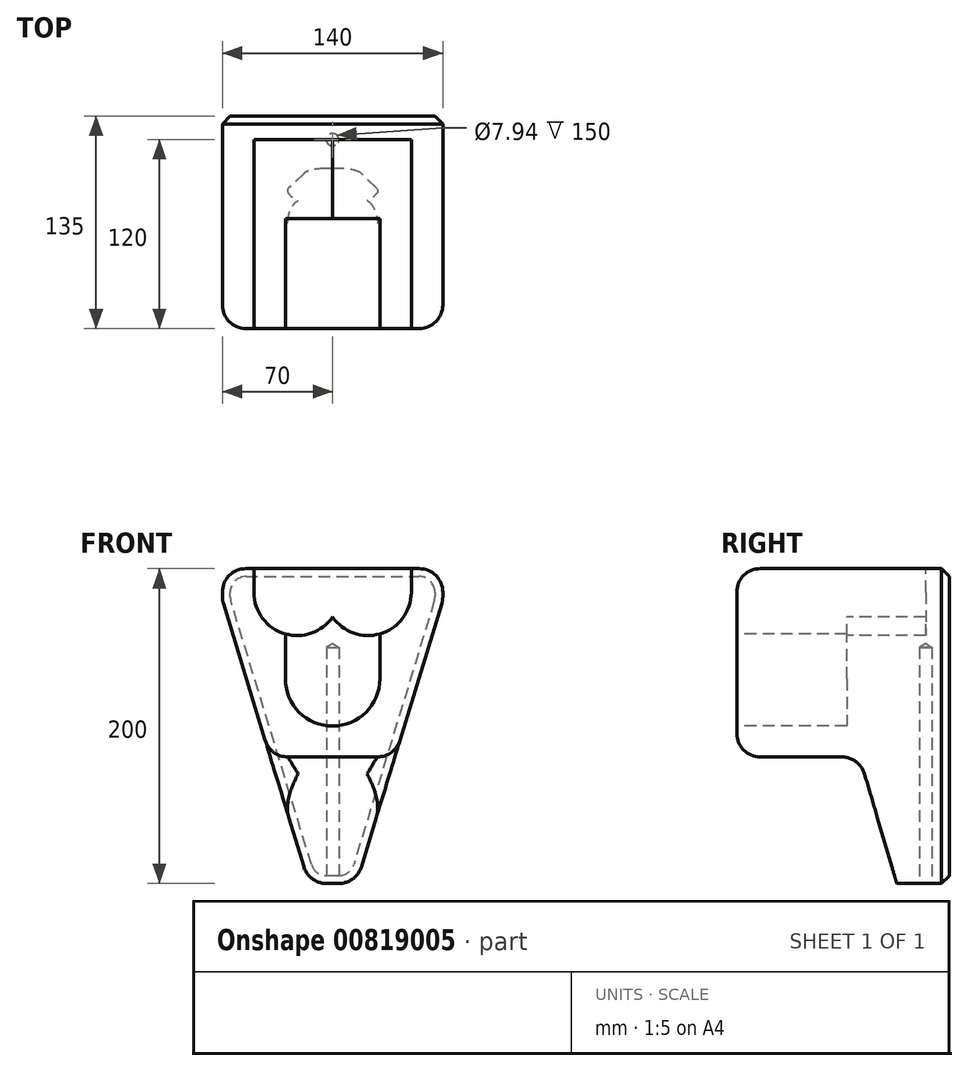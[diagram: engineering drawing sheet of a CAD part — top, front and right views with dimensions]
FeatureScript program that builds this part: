
annotation { "Feature Type Name" : "Feature", "Feature Type Description" : "" }
export const myFeature = defineFeature(function(context is Context, id is Id, definition is map)
    precondition{}
    {
        {
            var Q0;
            Q0=qCreatedBy(makeId("Front.planeOp"),FACE);
            var sketch = newSketch(context, id + "F0", { "sketchPlane" : qUnion([Q0])});
            skLineSegment(sketch, "E0.bottom", {"start": v(70, 70) * mm, "end": v(-70, 70) * mm});
            skLineSegment(sketch, "E0.left", {"start": v(70, 70) * mm, "end": v(70, 50) * mm});
            skLineSegment(sketch, "E0.right", {"start": v(-70, 70) * mm, "end": v(-70, 50) * mm});
            skPoint(sketch, "E0.middle", {"position": v(0, 60) * mm});
            skLineSegment(sketch, "E1", {"start": v(-70, 50) * mm, "end": v(-15, -130) * mm});
            skLineSegment(sketch, "E2", {"start": v(-15, -130) * mm, "end": v(15, -130) * mm});
            skLineSegment(sketch, "E3", {"start": v(15, -130) * mm, "end": v(70, 50) * mm});
            skSolve(sketch);
        }
        {
            var Q0;
            Q0=makeQuery(id+"F0.imprint","IMPRINT",FACE,{"disambiguationData":[TD([[makeQuery(id+"F0.imprint","IMPRINT",EDGE,{"derivedFrom":sQuery(id+"F0.wireOp",EDGE,"E0.bottom")}),1.0]])]});
            extrude(context, id + "F1", {"entities" : qUnion([Q0]), "depth" : 135 * mm, "offsetDistance" : 25 * mm});
        }
        {
            var Q0;
            Q0=makeQuery(id+"F1.opExtrude","CAP_FACE",FACE,{"disambiguationData":[OSD([sQuery(id+"F0.wireOp",EDGE,"E0.bottom"),sQuery(id+"F0.wireOp",EDGE,"E0.left"),sQuery(id+"F0.wireOp",EDGE,"E0.right"),sQuery(id+"F0.wireOp",EDGE,"E1"),sQuery(id+"F0.wireOp",EDGE,"E2"),sQuery(id+"F0.wireOp",EDGE,"E3")])],"isStart":false});
            var sketch = newSketch(context, id + "F2", { "sketchPlane" : qUnion([Q0])});
            skCircle(sketch, "E4", {"center": v(-22.5, 55) * mm, "radius": 27.5 * mm, "construction": true});
            skCircle(sketch, "E5.MirrorC", {"center": v(22.5, 55) * mm, "radius": 27.5 * mm, "construction": true});
            skLineSegment(sketch, "E6", {"start": v(-50, 55) * mm, "end": v(-50, 110) * mm});
            skLineSegment(sketch, "E7", {"start": v(-50, 110) * mm, "end": v(50, 110) * mm});
            skLineSegment(sketch, "E8", {"start": v(50, 110) * mm, "end": v(50, 55) * mm});
            skArc(sketch, "E9", {"start": v(-50, 55) * mm, "mid": v(-30.8, 28.78) * mm, "end": v(0, 39.19) * mm});
            skArc(sketch, "E10", {"start": v(0, 39.19) * mm, "mid": v(30.8, 28.78) * mm, "end": v(50, 55) * mm});
            skSolve(sketch);
        }
        {
            var Q0;
            Q0 = qSketchRegion(id + "F2", true);
            extrude(context, id + "F3", {"entities" : qUnion([Q0]), "operationType" : NewBodyOperationType.REMOVE, "oppositeDirection" : true, "depth" : 120 * mm, "offsetDistance" : 25 * mm});
        }
        {
            var Q0;
            Q0=makeQuery(id+"F1.opExtrude","SWEPT_EDGE",EDGE,{"disambiguationData":[OSD([sQuery(id+"F0.wireOp",EDGE,"E0.bottom"),sQuery(id+"F0.wireOp",EDGE,"E0.right")])]});
            var Q1;
            Q1=makeQuery(id+"F1.opExtrude","SWEPT_EDGE",EDGE,{"disambiguationData":[OSD([sQuery(id+"F0.wireOp",EDGE,"E0.bottom"),sQuery(id+"F0.wireOp",EDGE,"E0.left")])]});
            var Q2;
            Q2=makeQuery(id+"F1.opExtrude","SWEPT_EDGE",EDGE,{"disambiguationData":[OSD([sQuery(id+"F0.wireOp",EDGE,"E0.right"),sQuery(id+"F0.wireOp",EDGE,"E1")])]});
            var Q3;
            Q3=makeQuery(id+"F1.opExtrude","SWEPT_EDGE",EDGE,{"disambiguationData":[OSD([sQuery(id+"F0.wireOp",EDGE,"E0.left"),sQuery(id+"F0.wireOp",EDGE,"E3")])]});
            var Q4;
            Q4=makeQuery(id+"F1.opExtrude","SWEPT_EDGE",EDGE,{"disambiguationData":[OSD([sQuery(id+"F0.wireOp",EDGE,"E1"),sQuery(id+"F0.wireOp",EDGE,"E2")])]});
            var Q5;
            Q5=makeQuery(id+"F1.opExtrude","SWEPT_EDGE",EDGE,{"disambiguationData":[OSD([sQuery(id+"F0.wireOp",EDGE,"E2"),sQuery(id+"F0.wireOp",EDGE,"E3")])]});
            fillet(context, id + "F4", {"entities" : qUnion([Q0, Q1, Q2, Q3, Q4, Q5]), "radius" : 15 * mm, "tangentPropagation" : true, "allowEdgeOverflow" : false});
        }
        {
            var Q0;
            Q0=makeQuery(id+"F1.opExtrude","SWEPT_FACE",FACE,{"disambiguationData":[OSD([sQuery(id+"F0.wireOp",EDGE,"E2")])]});
            var sketch = newSketch(context, id + "F5", { "sketchPlane" : qUnion([Q0])});
            skCircle(sketch, "E11", {"center": v(0, 15) * mm, "radius": 7.5 * mm, "construction": true});
            skSolve(sketch);
        }
        {
            var Q0;
            Q0=sQuery(id+"F5.wireOp",VERTEX,"E11.center");
            var Q1;
            Q1=makeQuery(id+"F1.opExtrude","SWEPT_BODY",BODY,{"disambiguationData":[OSD([sQuery(id+"F0.wireOp",EDGE,"E0.bottom"),sQuery(id+"F0.wireOp",EDGE,"E0.left"),sQuery(id+"F0.wireOp",EDGE,"E0.right"),sQuery(id+"F0.wireOp",EDGE,"E1"),sQuery(id+"F0.wireOp",EDGE,"E2"),sQuery(id+"F0.wireOp",EDGE,"E3")])]});
            hole(context, id + "F6", {"style" : HoleStyle.SIMPLE, "endStyle" : HoleEndStyle.BLIND, "standardTappedOrClearance" : lookupTablePath({ "standard" : "ANSI", "engagement" : "75%", "pitch" : "16 tpi", "size" : "3/8", "type" : "Tapped" }), "standardBlindInLast" : lookupTablePath({ "standard" : "ANSI", "engagement" : "75%", "pitch" : "16 tpi", "size" : "3/8", "type" : "Tapped" }), "holeDiameter" : 7.94 * mm, "majorDiameter" : 9.52 * mm, "showTappedDepth" : true, "holeDepth" : 150 * mm, "isTappedThrough" : true, "tappedDepth" : 145.24 * mm, "tapClearance" : 3, "locations" : qUnion([Q0]), "scope" : qUnion([Q1])});
        }
        {
            var Q0;
            Q0=makeQuery(id+"F1.opExtrude","CAP_FACE",FACE,{"disambiguationData":[OSD([sQuery(id+"F0.wireOp",EDGE,"E0.bottom"),sQuery(id+"F0.wireOp",EDGE,"E0.left"),sQuery(id+"F0.wireOp",EDGE,"E0.right"),sQuery(id+"F0.wireOp",EDGE,"E1"),sQuery(id+"F0.wireOp",EDGE,"E2"),sQuery(id+"F0.wireOp",EDGE,"E3")])],"isStart":false});
            var sketch = newSketch(context, id + "F7", { "sketchPlane" : qUnion([Q0])});
            skCircle(sketch, "E12", {"center": v(0, 0) * mm, "radius": 30 * mm, "construction": true});
            skLineSegment(sketch, "E13", {"start": v(-30, 0) * mm, "end": v(-30, 100) * mm});
            skLineSegment(sketch, "E14", {"start": v(-30, 100) * mm, "end": v(30, 100) * mm});
            skLineSegment(sketch, "E15", {"start": v(30, 100) * mm, "end": v(30, 0) * mm});
            skArc(sketch, "E16", {"start": v(-30, 0) * mm, "mid": v(0, -30) * mm, "end": v(30, 0) * mm});
            skSolve(sketch);
        }
        {
            var Q0;
            Q0 = qSketchRegion(id + "F7", true);
            extrude(context, id + "F8", {"entities" : qUnion([Q0]), "operationType" : NewBodyOperationType.REMOVE, "oppositeDirection" : true, "depth" : 70 * mm, "offsetDistance" : 25 * mm});
        }
        {
            var Q0;
            Q0=qCreatedBy(makeId("Right.planeOp"),FACE);
            var sketch = newSketch(context, id + "F9", { "sketchPlane" : qUnion([Q0])});
            skLineSegment(sketch, "E17.bottom", {"start": v(-30.5, -139.58) * mm, "end": v(-175.25, -139.58) * mm});
            skLineSegment(sketch, "E18.bottom", {"start": v(-158.13, -49.6) * mm, "end": v(-57, -49.6) * mm});
            skLineSegment(sketch, "E19", {"start": v(-30.5, -139.58) * mm, "end": v(-57, -49.6) * mm});
            skLineSegment(sketch, "E20", {"start": v(-158.13, -49.6) * mm, "end": v(-175.25, -139.58) * mm});
            skSolve(sketch);
        }
        {
            var Q0;
            Q0=makeQuery(id+"F9.imprint","IMPRINT",FACE,{"disambiguationData":[TD([[makeQuery(id+"F9.imprint","IMPRINT",EDGE,{"derivedFrom":sQuery(id+"F9.wireOp",EDGE,"E17.bottom")}),-1.0]])]});
            extrude(context, id + "F10", {"entities" : qUnion([Q0]), "operationType" : NewBodyOperationType.REMOVE, "endBound" : BoundingType.THROUGH_ALL, "oppositeDirection" : true, "depth" : 25 * mm, "offsetDistance" : 25 * mm, "hasSecondDirection" : true, "secondDirectionBound" : SecondDirectionBoundingType.THROUGH_ALL, "secondDirectionOppositeDirection" : false, "secondDirectionDepth" : 25 * mm});
        }
        {
            var Q0;
            Q0=makeQuery(id+"F10.boolean.opBoolean","COPY",FACE,{"derivedFrom":makeQuery(id+"F10.opExtrude","SWEPT_FACE",FACE,{"disambiguationData":[OSD([sQuery(id+"F9.wireOp",EDGE,"E18.bottom")])]})});
            fillet(context, id + "F11", {"entities" : qUnion([Q0]), "radius" : 15 * mm, "tangentPropagation" : true, "allowEdgeOverflow" : false});
        }
        {
            var Q0;
            Q0=makeQuery(id+"F1.opExtrude","CAP_FACE",FACE,{"disambiguationData":[OSD([sQuery(id+"F0.wireOp",EDGE,"E0.bottom"),sQuery(id+"F0.wireOp",EDGE,"E0.left"),sQuery(id+"F0.wireOp",EDGE,"E0.right"),sQuery(id+"F0.wireOp",EDGE,"E1"),sQuery(id+"F0.wireOp",EDGE,"E2"),sQuery(id+"F0.wireOp",EDGE,"E3")])],"isStart":true});
            chamfer(context, id + "F12", {"entities" : qUnion([Q0]), "width" : 5 * mm, "tangentPropagation" : true});
        }
        {
            var Q0;
            {var subQ0=sQuery(id+"F0.wireOp",EDGE,"E0.left");var subQ1=sQuery(id+"F0.wireOp",EDGE,"E0.bottom");Q0=makeQuery(id+"F4.opFillet","BLEND_EDGE",EDGE,{"blendedFrom":[makeQuery(id+"F1.opExtrude","SWEPT_EDGE",EDGE,{"disambiguationData":[OSD([subQ1,subQ0])]}),makeQuery(id+"F1.opExtrude","CAP_FACE",FACE,{"disambiguationData":[OSD([subQ1,subQ0,sQuery(id+"F0.wireOp",EDGE,"E0.right"),sQuery(id+"F0.wireOp",EDGE,"E1"),sQuery(id+"F0.wireOp",EDGE,"E2"),sQuery(id+"F0.wireOp",EDGE,"E3")])],"isStart":false})],"blendedInto":[makeQuery(id+"F1.opExtrude","CAP_FACE",FACE,{"disambiguationData":[OSD([subQ1,subQ0,sQuery(id+"F0.wireOp",EDGE,"E0.right"),sQuery(id+"F0.wireOp",EDGE,"E1"),sQuery(id+"F0.wireOp",EDGE,"E2"),sQuery(id+"F0.wireOp",EDGE,"E3")])],"isStart":false})]});}
            var Q1;
            {var subQ0=sQuery(id+"F0.wireOp",EDGE,"E0.right");var subQ1=sQuery(id+"F0.wireOp",EDGE,"E0.bottom");Q1=makeQuery(id+"F4.opFillet","BLEND_EDGE",EDGE,{"blendedFrom":[makeQuery(id+"F1.opExtrude","SWEPT_EDGE",EDGE,{"disambiguationData":[OSD([subQ1,subQ0])]}),makeQuery(id+"F1.opExtrude","CAP_FACE",FACE,{"disambiguationData":[OSD([subQ1,sQuery(id+"F0.wireOp",EDGE,"E0.left"),subQ0,sQuery(id+"F0.wireOp",EDGE,"E1"),sQuery(id+"F0.wireOp",EDGE,"E2"),sQuery(id+"F0.wireOp",EDGE,"E3")])],"isStart":false})],"blendedInto":[makeQuery(id+"F1.opExtrude","CAP_FACE",FACE,{"disambiguationData":[OSD([subQ1,sQuery(id+"F0.wireOp",EDGE,"E0.left"),subQ0,sQuery(id+"F0.wireOp",EDGE,"E1"),sQuery(id+"F0.wireOp",EDGE,"E2"),sQuery(id+"F0.wireOp",EDGE,"E3")])],"isStart":false})]});}
            fillet(context, id + "F13", {"entities" : qUnion([Q0, Q1]), "radius" : 15 * mm, "tangentPropagation" : true, "allowEdgeOverflow" : false});
        }
    });
